# Revit family: S0400TAL
name_source: partatom
category: Lighting Fixtures
revit_build: Autodesk Revit 2017 (Build: 20160225_1515(x64)
units: mm (PartAtom-declared; Revit-internal decimal feet)

## family parameters
Cut with Voids When Loaded = No
Host = Face
Light Source = Yes
Part Type = Normal
Room Calculation Point = No
Round Connector Dimension = Use Diameter
Shared = No

## types (1)
- STAL.0400.99.40.90
    Apparent Load = 99 VA
    Color Filter = 16777215
    Default Elevation = 1219 mm
    Description = 99W - 90°
    Dimming Lamp Color Temperature Shift = <None>
    Emit Shape Visible in Rendering = No
    Emit from Rectangle Length = 416 mm
    Emit from Rectangle Width = 180 mm  [stored 0.590551 ft]
    Lamp = LED
    Manufacturer = ARLIGHT
    Model = S0400TAL
    Photometric Web File = s-0400-tal-99w-4k-80ra-90d.ies
    Tilt Angle = -90.00°
    Type Comments = Industrial Lighting
    Type Image = talia-header.jpg
    URL = http://www.arlight.net
    Wattage Comments = 99W

note: [stored X ft] marks values corroborated as IEEE doubles in the binary element streams (Revit-internal decimal feet)

## geometry (parser evidence)
native form markers: Sweep x3
no freeform markers — native parametric forms only
